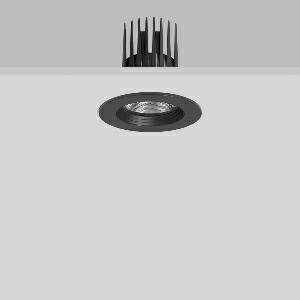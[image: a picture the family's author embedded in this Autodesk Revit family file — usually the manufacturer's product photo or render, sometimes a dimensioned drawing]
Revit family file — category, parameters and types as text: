
# Revit family: heledon_mini_e_901750_003_1_76_832b
name_source: partatom
category: Lighting Fixtures
units: mm (PartAtom-declared; Revit-internal decimal feet)

## family parameters
Cut with Voids When Loaded = No
Host = Face
Light Source = No
Part Type = Normal
Room Calculation Point = No
Round Connector Dimension = Use Diameter
Shared = No

## types (1)
- HELEDON mini E (1 x LED Modul 940, 3900 lm, 4000)
    Apparent Load = 29 VA
    Approval mark = CE
    CIE Flux Codes = 95 99 100 100 100
    Color Rendering = 92
    Color Temperature = 4000
    Default Elevation = 1800 mm
    Description = Series: HELEDON mini
Round recessed downlight. Housing: die-cast aluminium, powder-coated. Black plastic ring and recessed LED to prevent glare from the side. Optical assembly with reflector made of MIRO-Silver with 98% total light reflection for outstanding efficiency - can be changed without tools. Best colour rendering index Ra>90. Suitable for Recessed ceiling mounting. Installation without tools thanks to spring fastening system. Including separate LED converter with connecting cable 600 mm.High quality converter without flickering and stroboscopic effect. Through-wiring box (5 pole) available as accessory. The following accessories can be mounted without use of tools: interchangeable lenses, decorative glasses, honeycomb louvre, clear and frosted diffusers, white interchangeable plastic ring. 
Colour: deep black, matt (RAL 9005)
Diameter: 124 mm
Height: 3 mm
Cut-out diameter: 114 mm
Recess height: 170 mm
Luminaire: recess height: 120 mm
Lamp: LED
Socket: without socket
Colour temperature: 4000K
Colour rendering index (CRI): 92
System power: 29 W
Rated luminous flux: 3900 lm
Luminous efficiency: 134 lm/W
Control gear: Converter, dimmable, DALI
Protection class: II
Type of protection: IP 20
    Height = 0 mm  [stored 0 ft]
    Lamp = 1 x LED Modul 940
    Lamp Light Flux = 3900 lm
    Lamp count = 1
    Length = 124 mm  [stored 0.406824 ft]
    Lifetime = 50000 h
    Luminous efficacy = 134 lm/W
    Manufacturer = RZB
    ModVariant = No
    Model = 901750.003.1.76
    Mounting Place = Ceiling
    Mounting Type = Recessed
    Number of Poles = 1
    OnlyDefault = Yes
    Power Factor = 1
    Product Name = HELEDON mini E
    Product group = Recessed downlights
    ProductGroupID = 402
    Protection Class = Protection class II
    Protection Degree = IP 20
    RLX_Detail_Level = 1
    RLX_Emergency_Light_Flux = 0 lm
    RLX_Emergency_Type = 0
    RLX_Emergency_Type_DB = No
    RlxData = <blob elided: 128437 chars, md5=f6034b71>
    Socket = socket
    Standby Power = 0 W
    System Light Flux = 3900 lm
    System Power = 29 W
    Type Comments = Product without accessories
    Type Image = 901657.003.jpg
    URL = http://relux.com
    VarID = ---
    Voltage = 230 V
    Voltage Range = 220-240 V
    Weight = 0.00 kg
    Width = 0 mm  [stored 0 ft]

note: [stored X ft] marks values corroborated as IEEE doubles in the binary element streams (Revit-internal decimal feet)

## geometry (parser evidence)
native form markers: Blend x4, Sweep x10
no freeform markers — native parametric forms only
